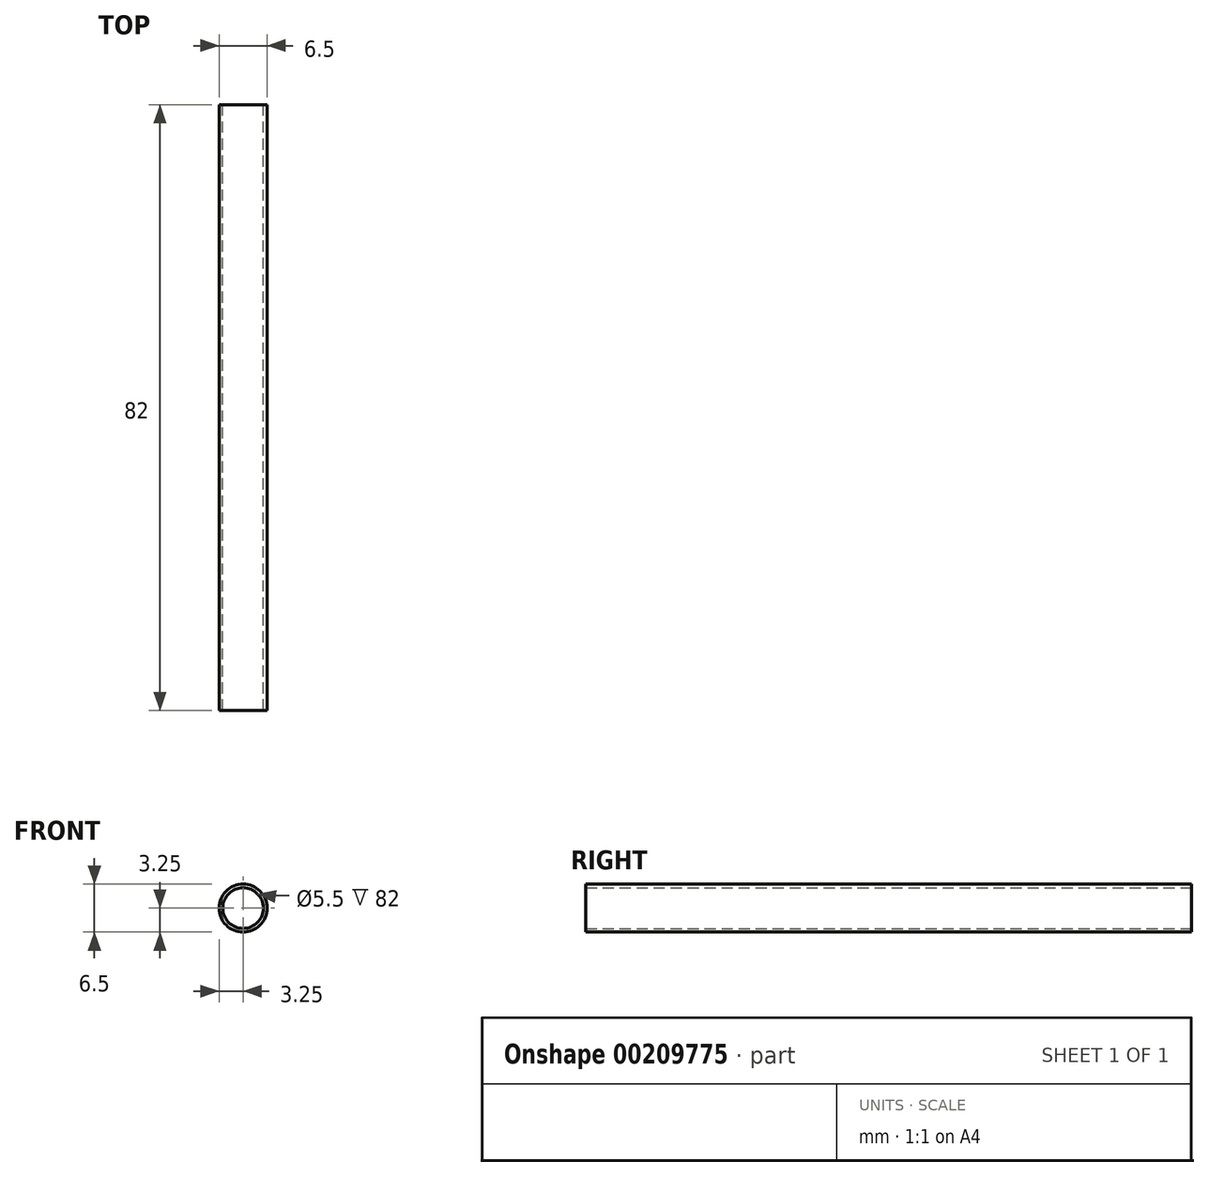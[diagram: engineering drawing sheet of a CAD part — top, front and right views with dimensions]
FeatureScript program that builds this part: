
annotation { "Feature Type Name" : "Feature", "Feature Type Description" : "" }
export const myFeature = defineFeature(function(context is Context, id is Id, definition is map)
    precondition{}
    {
        {
            var Q0;
            Q0=qCreatedBy(makeId("Front.planeOp"),FACE);
            var sketch = newSketch(context, id + "F0", { "sketchPlane" : qUnion([Q0])});
            skCircle(sketch, "E0", {"center": v(0, 0) * mm, "radius": 3.25 * mm});
            skCircle(sketch, "E1", {"center": v(0, 0) * mm, "radius": 2.75 * mm});
            skSolve(sketch);
        }
        {
            var Q0;
            Q0 = qSketchRegion(id + "F0", true);
            extrude(context, id + "F1", {"entities" : qUnion([Q0]), "depth" : 82 * mm});
        }
    });
